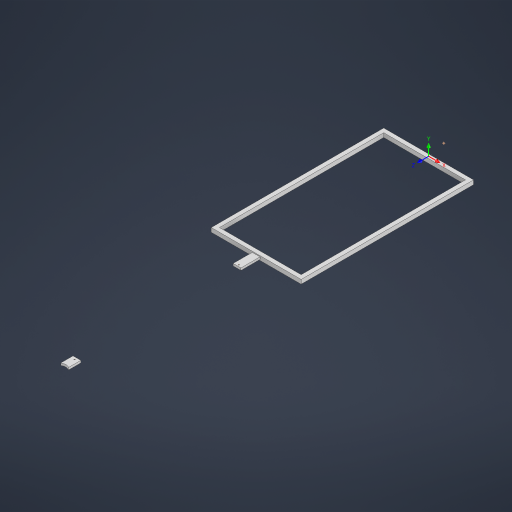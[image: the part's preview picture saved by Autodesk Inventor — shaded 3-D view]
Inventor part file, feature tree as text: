
AUTODESK INVENTOR PART (.ipt)
format: ipt  version: 2024 (Build 280153000, 153)  size: 240,128 bytes
history: native  units: mm
features: other x13, sketch x5, extrude x4, plane x1
ambient origin geometry x8: Origin, YZ Plane, XZ Plane, XY Plane, X Axis, Y Axis, Z Axis, Center Point
bodies: Body1 (feature_tree)
feature tree (23):
  other  "Sólido1"
  sketch  "Boceto2"  dims[d16=105.8mm d17=81.0mm]
  extrude  "Extrusión1"  Depth=81.0mm
  extrude  "Extrusión2"  Depth=28.4mm
  extrude  "Extrusión3"  Depth=150.0mm
  extrude  "Extrusión4"  TaperAngle=0.0deg  [1 undecoded]
  plane  "Plano de trabajo1"
  sketch  "Boceto5"  dims[d23=150.0mm d24=0.0mm]
  other  "Punto de trabajo1"
  other  "Punto de trabajo2"
  other  "Punto de trabajo3"
  other  "Punto de trabajo4"
  sketch  "Boceto6"  dims[d25=15.0mm d26=0.0mm d27=8.0mm d28=0.0mm d29=15.0mm d30=15.0mm d31=15.0mm d32=15.0mm d33=15.0mm d34=0.0mm d35=70.0mm d36=45.0mm d37=4.0mm d38=4.0mm d39=15.0mm d40=0.0mm d41=164.2mm d42=7.5mm d43=0.0mm d44=0.0mm d45=0.0mm d46=0.0mm d47=0.0mm d48=0.0mm d49=630.0mm]
  other  "SCU1"
  sketch  "Boceto3"  dims[d18=700.0mm d19=28.4mm]
  sketch  "Boceto4"  dims[d21=630.0mm d22=150.0mm]
  other  "SCU1: Plano YZ"
  other  "SCU1: Plano XZ"
  other  "SCU1: Plano XY"
  other  "SCU1: Eje X"
  other  "SCU1: Eje Y"
  other  "SCU1: Eje Z"
  other  "SCU1: Centro"
note: 1 required parameter value undecoded (feature->parameter linkage not recoverable at this tier; creation-order binding heuristic only, values carry confidence <= 0.55)
